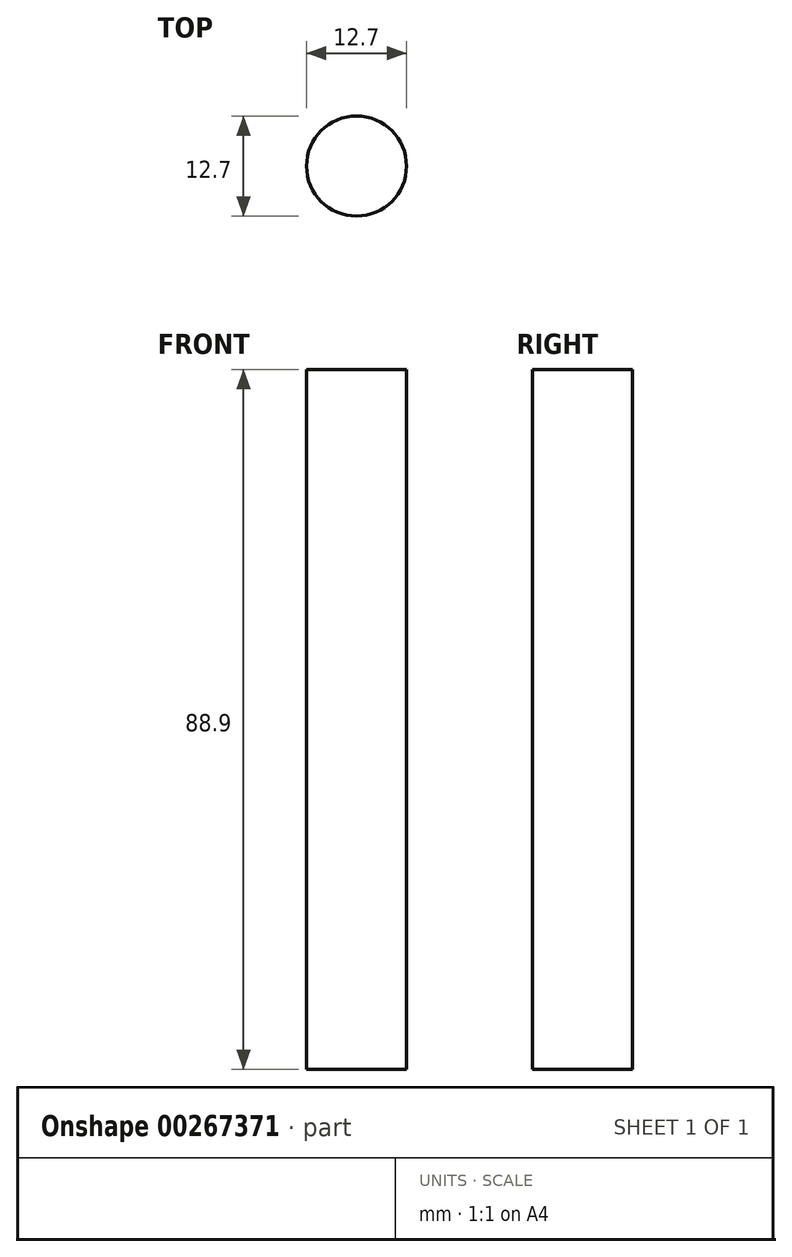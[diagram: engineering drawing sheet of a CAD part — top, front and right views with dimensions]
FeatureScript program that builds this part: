
annotation { "Feature Type Name" : "Feature", "Feature Type Description" : "" }
export const myFeature = defineFeature(function(context is Context, id is Id, definition is map)
    precondition{}
    {
        {
            var Q0;
            Q0=qCreatedBy(makeId("Top.planeOp"),FACE);
            var sketch = newSketch(context, id + "F0", { "sketchPlane" : qUnion([Q0])});
            skCircle(sketch, "E0", {"center": v(0, 0.3) * mm, "radius": 6.35 * mm});
            skSolve(sketch);
        }
        {
            var Q0;
            Q0=makeQuery(id+"F0.imprint","IMPRINT",FACE,{"disambiguationData":[TD([[makeQuery(id+"F0.imprint","IMPRINT",EDGE,{"derivedFrom":sQuery(id+"F0.wireOp",EDGE,"E0")}),1.0]])]});
            extrude(context, id + "F1", {"entities" : qUnion([Q0]), "depth" : 88.9 * mm});
        }
    });
